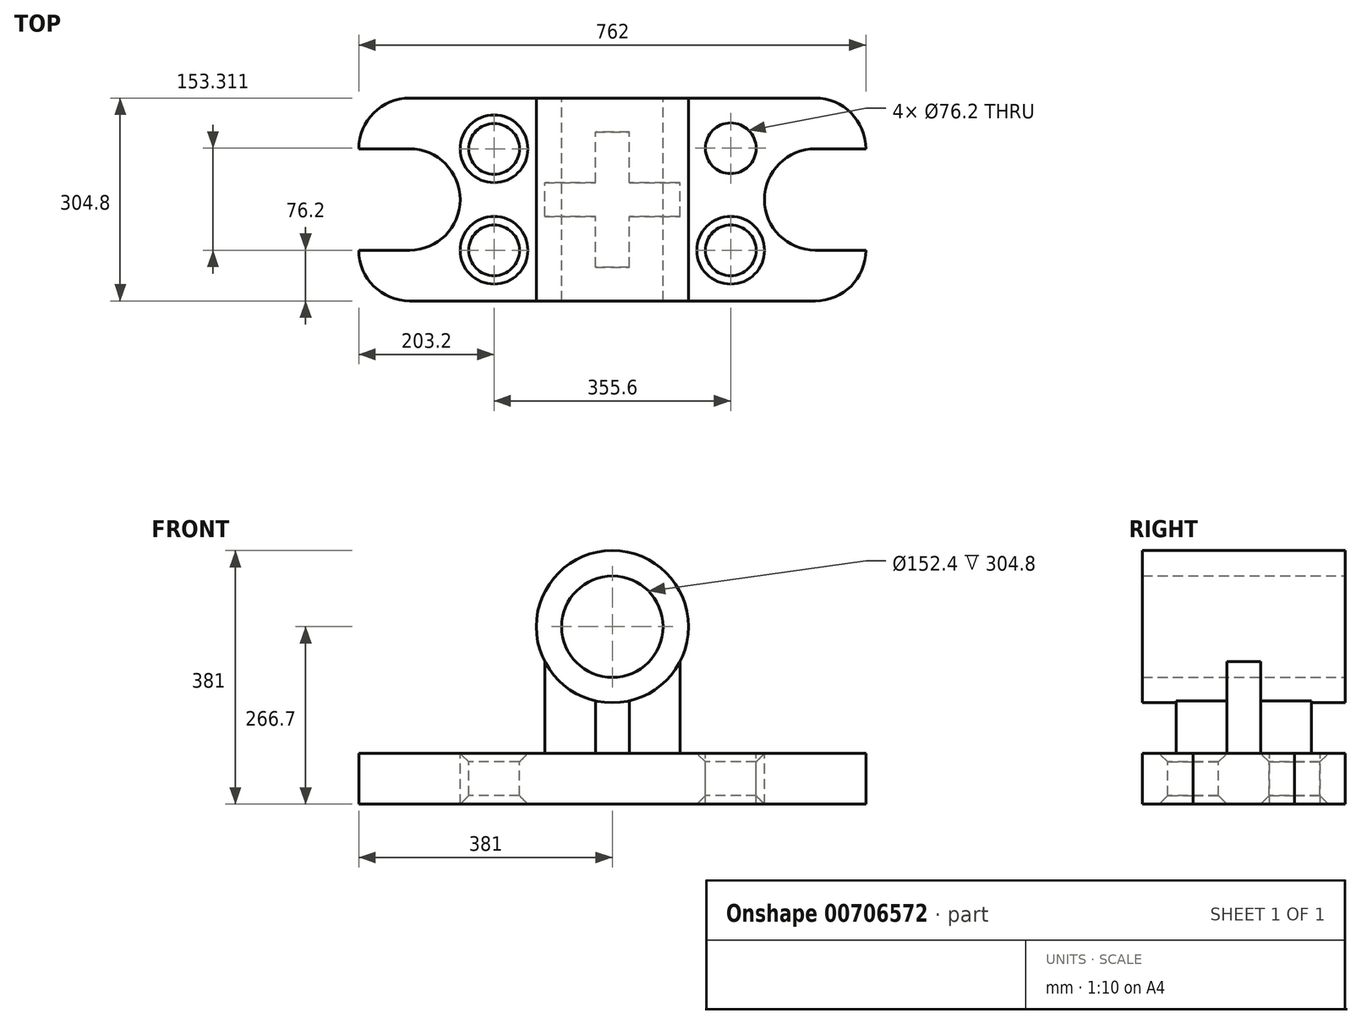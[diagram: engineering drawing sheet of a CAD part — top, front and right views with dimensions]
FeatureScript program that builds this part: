
annotation { "Feature Type Name" : "Feature", "Feature Type Description" : "" }
export const myFeature = defineFeature(function(context is Context, id is Id, definition is map)
    precondition{}
    {
        {
            var Q0;
            Q0=qCreatedBy(makeId("Top.planeOp"),FACE);
            var sketch = newSketch(context, id + "F0", { "sketchPlane" : qUnion([Q0])});
            skLineSegment(sketch, "E0", {"start": v(-304.8, 0) * mm, "end": v(304.8, 0) * mm});
            skLineSegment(sketch, "E1", {"start": v(304.8, -304.8) * mm, "end": v(-304.8, -304.8) * mm});
            skPoint(sketch, "E2.visualSharp", {"position": v(-381, 0) * mm});
            skArc(sketch, "E2.filletArc", {"start": v(-304.8, 0) * mm, "mid": v(-358.68, -22.32) * mm, "end": v(-381, -76.2) * mm});
            skPoint(sketch, "E3.visualSharp", {"position": v(-381, -304.8) * mm});
            skArc(sketch, "E3.filletArc", {"start": v(-381, -228.6) * mm, "mid": v(-358.68, -282.48) * mm, "end": v(-304.8, -304.8) * mm});
            skPoint(sketch, "E4.visualSharp", {"position": v(381, 0) * mm});
            skArc(sketch, "E4.filletArc", {"start": v(381, -76.2) * mm, "mid": v(358.68, -22.32) * mm, "end": v(304.8, 0) * mm});
            skArc(sketch, "E5.filletArc", {"start": v(304.8, -304.8) * mm, "mid": v(358.68, -282.48) * mm, "end": v(381, -228.6) * mm});
            skLineSegment(sketch, "E6", {"start": v(-381, -76.2) * mm, "end": v(-304.8, -76.2) * mm});
            skLineSegment(sketch, "E7", {"start": v(-381, -228.6) * mm, "end": v(-304.8, -228.6) * mm});
            skArc(sketch, "E8", {"start": v(-304.8, -228.6) * mm, "mid": v(-228.6, -152.4) * mm, "end": v(-304.8, -76.2) * mm});
            skLineSegment(sketch, "E9.MirrorCS", {"start": v(381, -76.2) * mm, "end": v(304.8, -76.2) * mm});
            skArc(sketch, "E10.MirrorCS", {"start": v(304.8, -228.6) * mm, "mid": v(228.6, -152.4) * mm, "end": v(304.8, -76.2) * mm});
            skLineSegment(sketch, "E11.MirrorCS", {"start": v(381, -228.6) * mm, "end": v(304.8, -228.6) * mm});
            skCircle(sketch, "E12", {"center": v(-177.8, -76.2) * mm, "radius": 38.1 * mm});
            skCircle(sketch, "E13", {"center": v(-177.8, -228.6) * mm, "radius": 38.1 * mm});
            skCircle(sketch, "E14", {"center": v(177.8, -75.29) * mm, "radius": 38.1 * mm});
            skCircle(sketch, "E15", {"center": v(177.8, -228.6) * mm, "radius": 38.1 * mm});
            skLineSegment(sketch, "E16", {"start": v(-25.4, -48.3) * mm, "end": v(25.4, -48.3) * mm});
            skLineSegment(sketch, "E17", {"start": v(25.4, -48.3) * mm, "end": v(25.4, -114.88) * mm});
            skLineSegment(sketch, "E18", {"start": v(25.4, -114.88) * mm, "end": v(101.6, -114.88) * mm});
            skLineSegment(sketch, "E19", {"start": v(101.6, -114.88) * mm, "end": v(101.6, -165.68) * mm});
            skLineSegment(sketch, "E20", {"start": v(101.6, -165.68) * mm, "end": v(25.4, -165.68) * mm});
            skLineSegment(sketch, "E21", {"start": v(25.4, -165.68) * mm, "end": v(25.4, -241.88) * mm});
            skLineSegment(sketch, "E22", {"start": v(25.4, -241.88) * mm, "end": v(-25.4, -241.88) * mm});
            skLineSegment(sketch, "E23", {"start": v(-25.4, -241.88) * mm, "end": v(-25.4, -165.68) * mm});
            skLineSegment(sketch, "E24", {"start": v(-25.4, -165.68) * mm, "end": v(-101.6, -165.68) * mm});
            skLineSegment(sketch, "E25", {"start": v(-101.6, -165.68) * mm, "end": v(-101.6, -114.88) * mm});
            skLineSegment(sketch, "E26", {"start": v(-101.6, -114.88) * mm, "end": v(-25.4, -114.88) * mm});
            skLineSegment(sketch, "E27", {"start": v(-25.4, -114.88) * mm, "end": v(-25.4, -48.3) * mm});
            skSolve(sketch);
        }
        {
            var Q0;
            Q0=makeQuery(id+"F0.imprint","IMPRINT",FACE,{"disambiguationData":[TD([[makeQuery(id+"F0.imprint","IMPRINT",EDGE,{"derivedFrom":sQuery(id+"F0.wireOp",EDGE,"E0")}),-1.0]])]});
            var Q1;
            Q1=makeQuery(id+"F0.imprint","IMPRINT",FACE,{"disambiguationData":[TD([[makeQuery(id+"F0.imprint","IMPRINT",EDGE,{"derivedFrom":sQuery(id+"F0.wireOp",EDGE,"E12")}),1.0]])]});
            var Q2;
            Q2=makeQuery(id+"F0.imprint","IMPRINT",FACE,{"disambiguationData":[TD([[makeQuery(id+"F0.imprint","IMPRINT",EDGE,{"derivedFrom":sQuery(id+"F0.wireOp",EDGE,"E16")}),-1.0]])]});
            var Q3;
            Q3=makeQuery(id+"F0.imprint","IMPRINT",FACE,{"disambiguationData":[TD([[makeQuery(id+"F0.imprint","IMPRINT",EDGE,{"derivedFrom":sQuery(id+"F0.wireOp",EDGE,"E14")}),1.0]])]});
            var Q4;
            Q4=makeQuery(id+"F0.imprint","IMPRINT",FACE,{"disambiguationData":[TD([[makeQuery(id+"F0.imprint","IMPRINT",EDGE,{"derivedFrom":sQuery(id+"F0.wireOp",EDGE,"E15")}),1.0]])]});
            var Q5;
            Q5=makeQuery(id+"F0.imprint","IMPRINT",FACE,{"disambiguationData":[TD([[makeQuery(id+"F0.imprint","IMPRINT",EDGE,{"derivedFrom":sQuery(id+"F0.wireOp",EDGE,"E13")}),1.0]])]});
            extrude(context, id + "F1", {"entities" : qUnion([Q0, Q1, Q2, Q3, Q4, Q5]), "oppositeDirection" : true, "depth" : 76.2 * mm, "offsetDistance" : 25.4 * mm});
        }
        {
            var Q0;
            Q0=qCreatedBy(makeId("Top.planeOp"),FACE);
            var sketch = newSketch(context, id + "F2", { "sketchPlane" : qUnion([Q0])});
            skLineSegment(sketch, "E28.bottom", {"start": v(-25.4, -50.8) * mm, "end": v(25.4, -50.8) * mm});
            skLineSegment(sketch, "E28.top", {"start": v(-25.4, -254) * mm, "end": v(25.4, -254) * mm});
            skLineSegment(sketch, "E28.left", {"start": v(-101.6, -127) * mm, "end": v(-101.6, -177.8) * mm});
            skLineSegment(sketch, "E28.right", {"start": v(101.6, -127) * mm, "end": v(101.6, -177.8) * mm});
            skPoint(sketch, "E28.middle", {"position": v(0, -152.4) * mm});
            skLineSegment(sketch, "E29.0", {"start": v(-25.4, -50.8) * mm, "end": v(-25.4, -127) * mm});
            skLineSegment(sketch, "E30.0", {"start": v(25.4, -50.8) * mm, "end": v(25.4, -127) * mm});
            skLineSegment(sketch, "E31.0", {"start": v(-101.6, -127) * mm, "end": v(-25.4, -127) * mm});
            skLineSegment(sketch, "E32.0", {"start": v(-101.6, -177.8) * mm, "end": v(-25.4, -177.8) * mm});
            skLineSegment(sketch, "E33.trimOffspring", {"start": v(25.4, -127) * mm, "end": v(101.6, -127) * mm});
            skLineSegment(sketch, "E34.trimOffspring", {"start": v(-25.4, -177.8) * mm, "end": v(-25.4, -254) * mm});
            skLineSegment(sketch, "E35.trimOffspring", {"start": v(25.4, -177.8) * mm, "end": v(101.6, -177.8) * mm});
            skLineSegment(sketch, "E36.trimOffspring", {"start": v(25.4, -177.8) * mm, "end": v(25.4, -254) * mm});
            skPoint(sketch, "E37.orphan", {"position": v(101.6, -50.8) * mm});
            skPoint(sketch, "E38.orphan", {"position": v(101.6, -254) * mm});
            skPoint(sketch, "E39.orphan", {"position": v(-101.6, -254) * mm});
            skPoint(sketch, "E40.orphan", {"position": v(-101.6, -50.8) * mm});
            skCircle(sketch, "E41", {"center": v(-177.8, -76.2) * mm, "radius": 38.1 * mm});
            skCircle(sketch, "E42", {"center": v(-177.8, -228.6) * mm, "radius": 38.1 * mm});
            skCircle(sketch, "E43.MirrorC", {"center": v(177.8, -76.2) * mm, "radius": 38.1 * mm});
            skCircle(sketch, "E44.MirrorC", {"center": v(177.8, -228.6) * mm, "radius": 38.1 * mm});
            skSolve(sketch);
        }
        {
            var Q0;
            Q0=makeQuery(id+"F2.imprint","IMPRINT",FACE,{"disambiguationData":[TD([[makeQuery(id+"F2.imprint","IMPRINT",EDGE,{"derivedFrom":sQuery(id+"F2.wireOp",EDGE,"E28.bottom")}),-1.0]])]});
            extrude(context, id + "F3", {"entities" : qUnion([Q0]), "operationType" : NewBodyOperationType.ADD, "depth" : 175 * mm, "offsetDistance" : 25.4 * mm});
        }
        {
            var Q0;
            Q0=qCreatedBy(makeId("Front.planeOp"),FACE);
            var sketch = newSketch(context, id + "F4", { "sketchPlane" : qUnion([Q0])});
            skLineSegment(sketch, "E45", {"start": v(0, 0) * mm, "end": v(0, 190.5) * mm});
            skCircle(sketch, "E46", {"center": v(0, 190.5) * mm, "radius": 76.2 * mm});
            skCircle(sketch, "E47", {"center": v(0, 190.5) * mm, "radius": 114.3 * mm});
            skSolve(sketch);
        }
        {
            var Q0;
            Q0=makeQuery(id+"F4.imprint","IMPRINT",FACE,{"disambiguationData":[TD([[makeQuery(id+"F4.imprint","IMPRINT",EDGE,{"derivedFrom":sQuery(id+"F4.wireOp",EDGE,"E46")}),-1.0]])]});
            var Q1;
            Q1=makeQuery(id+"F4.imprint","IMPRINT",FACE,{"disambiguationData":[TD([[makeQuery(id+"F4.imprint","IMPRINT",EDGE,{"derivedFrom":sQuery(id+"F4.wireOp",EDGE,"E46")}),1.0]])]});
            extrude(context, id + "F5", {"entities" : qUnion([Q0, Q1]), "operationType" : NewBodyOperationType.ADD, "depth" : 304.8 * mm, "offsetDistance" : 25.4 * mm});
        }
        {
            var Q0;
            Q0=makeQuery(id+"F4.imprint","IMPRINT",FACE,{"disambiguationData":[TD([[makeQuery(id+"F4.imprint","IMPRINT",EDGE,{"derivedFrom":sQuery(id+"F4.wireOp",EDGE,"E46")}),1.0]])]});
            extrude(context, id + "F6", {"entities" : qUnion([Q0]), "operationType" : NewBodyOperationType.REMOVE, "depth" : 430.02 * mm, "offsetDistance" : 25.4 * mm});
        }
        {
            var Q0;
            Q0=makeQuery(id+"F0.imprint","IMPRINT",FACE,{"disambiguationData":[TD([[makeQuery(id+"F0.imprint","IMPRINT",EDGE,{"derivedFrom":sQuery(id+"F0.wireOp",EDGE,"E12")}),1.0]])]});
            var Q1;
            Q1=makeQuery(id+"F0.imprint","IMPRINT",FACE,{"disambiguationData":[TD([[makeQuery(id+"F0.imprint","IMPRINT",EDGE,{"derivedFrom":sQuery(id+"F0.wireOp",EDGE,"E13")}),1.0]])]});
            var Q2;
            Q2=makeQuery(id+"F0.imprint","IMPRINT",FACE,{"disambiguationData":[TD([[makeQuery(id+"F0.imprint","IMPRINT",EDGE,{"derivedFrom":sQuery(id+"F0.wireOp",EDGE,"E14")}),1.0]])]});
            var Q3;
            Q3=makeQuery(id+"F0.imprint","IMPRINT",FACE,{"disambiguationData":[TD([[makeQuery(id+"F0.imprint","IMPRINT",EDGE,{"derivedFrom":sQuery(id+"F0.wireOp",EDGE,"E15")}),1.0]])]});
            extrude(context, id + "F7", {"entities" : qUnion([Q0, Q1, Q2, Q3]), "operationType" : NewBodyOperationType.REMOVE, "oppositeDirection" : true, "depth" : 172.72 * mm, "offsetDistance" : 25.4 * mm});
        }
        {
            var Q0;
            Q0=makeQuery(id+"F7.boolean.opBoolean","COPY",EDGE,{"derivedFrom":makeQuery(id+"F7.opExtrude","CAP_EDGE",EDGE,{"disambiguationData":[OSD([sQuery(id+"F0.wireOp",EDGE,"E14")])],"isStart":true})});
            var Q1;
            Q1=makeQuery(id+"F7.boolean.opBoolean","COPY",FACE,{"derivedFrom":makeQuery(id+"F7.opExtrude","SWEPT_FACE",FACE,{"disambiguationData":[OSD([sQuery(id+"F0.wireOp",EDGE,"E15")])]})});
            var Q2;
            Q2=makeQuery(id+"F7.boolean.opBoolean","COPY",FACE,{"derivedFrom":makeQuery(id+"F7.opExtrude","SWEPT_FACE",FACE,{"disambiguationData":[OSD([sQuery(id+"F0.wireOp",EDGE,"E13")])]})});
            var Q3;
            Q3=makeQuery(id+"F7.boolean.opBoolean","COPY",FACE,{"derivedFrom":makeQuery(id+"F7.opExtrude","SWEPT_FACE",FACE,{"disambiguationData":[OSD([sQuery(id+"F0.wireOp",EDGE,"E12")])]})});
            chamfer(context, id + "F8", {"entities" : qUnion([Q0, Q1, Q2, Q3]), "width" : 12.7 * mm, "tangentPropagation" : true});
        }
    });
